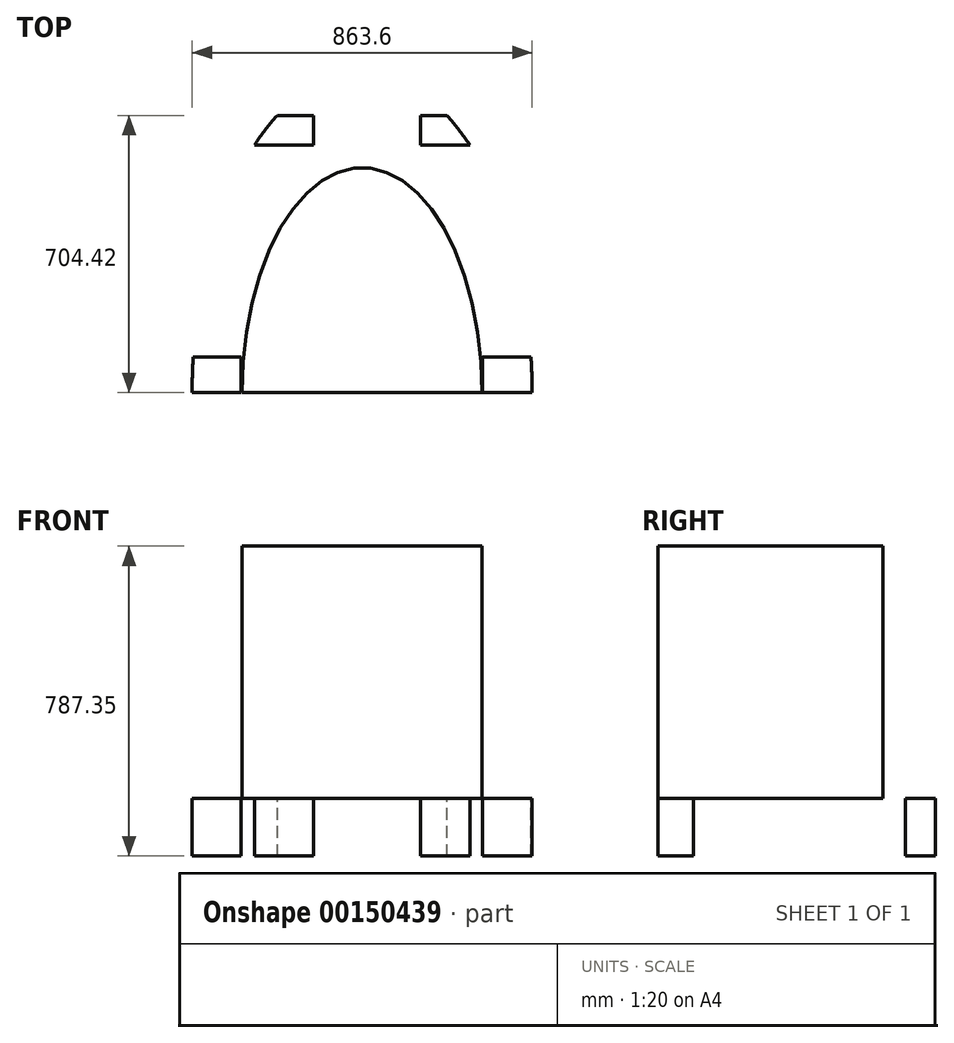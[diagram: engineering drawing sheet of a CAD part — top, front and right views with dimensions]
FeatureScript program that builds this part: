
annotation { "Feature Type Name" : "Feature", "Feature Type Description" : "" }
export const myFeature = defineFeature(function(context is Context, id is Id, definition is map)
    precondition{}
    {
        {
            var Q0;
            Q0=qCreatedBy(makeId("Top.planeOp"),FACE);
            var sketch = newSketch(context, id + "F0", { "sketchPlane" : qUnion([Q0])});
            skLineSegment(sketch, "E0", {"start": v(-431.8, 0) * mm, "end": v(431.8, 0) * mm});
            skEllipticalArc(sketch, "E1", {});
            skPoint(sketch, "E2", {"position": v(0, 812.8) * mm});
            skPoint(sketch, "E3", {"position": v(-304.8, 0) * mm});
            skPoint(sketch, "E4", {"position": v(304.8, 0) * mm});
            skPoint(sketch, "E5", {"position": v(0, 571.5) * mm});
            const initialGuessF0  = {"E1": [0, 0, 0, 1, 0.8128, 0.4318, 4.71238898038469, 1.5707963267948966], "E1": [0, 0, 0, 1, 0.5715, 0.3048, 4.71238898038469, 1.5707963267948966]};
            skSetInitialGuess(sketch, initialGuessF0);
            skSolve(sketch);
        }
        {
            var Q0;
            {var subQ0=sQuery(id+"F0.wireOp",EDGE,"E1");Q0=makeQuery(id+"F0.imprint","IMPRINT",FACE,{"disambiguationData":[TD([[makeQuery(id+"F0.imprint","IMPRINT",EDGE,{"derivedFrom":subQ0}),1.0]])]});}
            extrude(context, id + "F1", {"entities" : qUnion([Q0]), "depth" : 787.4 * mm - 501.65 * mm});
        }
        {
            var Q0;
            Q0 = qSketchRegion(id + "F0", true);
            extrude(context, id + "F2", {"entities" : qUnion([Q0]), "operationType" : NewBodyOperationType.ADD, "oppositeDirection" : true, "depth" : 355.6 * mm});
        }
        {
            var Q0;
            Q0=makeQuery(id+"F2.opExtrude","CAP_FACE",FACE,{"disambiguationData":[OSD([sQuery(id+"F0.wireOp",EDGE,"bZ2ABtPo-rZ60-tPIg-W25j-avqFfYisGgns"),sQuery(id+"F0.wireOp",EDGE,"E0")])],"isStart":false});
            var sketch = newSketch(context, id + "F3", { "sketchPlane" : qUnion([Q0])});
            skEllipticalArc(sketch, "E6.0", {});
            skLineSegment(sketch, "E7.0", {"start": v(-431.8, 0) * mm, "end": v(-307.65, 0) * mm});
            skLineSegment(sketch, "E8", {"start": v(-429.13, -90.23) * mm, "end": v(-307.65, -90.23) * mm});
            skLineSegment(sketch, "E9", {"start": v(306.2, 0) * mm, "end": v(306.2, -90.23) * mm});
            skLineSegment(sketch, "E10", {"start": v(-307.65, 0) * mm, "end": v(-307.65, -90.23) * mm});
            skLineSegment(sketch, "E11", {"start": v(215.43, -704.42) * mm, "end": v(147.86, -704.42) * mm});
            skLineSegment(sketch, "E12", {"start": v(273.47, -629) * mm, "end": v(147.86, -629) * mm});
            skLineSegment(sketch, "E13", {"start": v(-123.88, -704.42) * mm, "end": v(-123.88, -629) * mm});
            skLineSegment(sketch, "E14", {"start": v(147.86, -704.42) * mm, "end": v(147.86, -629) * mm});
            skLineSegment(sketch, "E15.trimOffspring", {"start": v(306.2, 0) * mm, "end": v(431.8, 0) * mm});
            skLineSegment(sketch, "E16.trimOffspring", {"start": v(306.2, -90.23) * mm, "end": v(429.13, -90.23) * mm});
            skEllipticalArc(sketch, "E17.trimOffspring", {});
            skEllipticalArc(sketch, "E18.trimOffspring", {});
            skLineSegment(sketch, "E19.trimOffspring", {"start": v(-123.88, -629) * mm, "end": v(-273.47, -629) * mm});
            skLineSegment(sketch, "E20.trimOffspring", {"start": v(-123.88, -704.42) * mm, "end": v(-215.43, -704.42) * mm});
            skEllipticalArc(sketch, "E21.trimOffspring", {});
            const initialGuessF3  = {"E6.0": [0, 0, 0, -1, 0.8128, 0.4318, 4.71238898038469, 4.823633551072674], "E17.trimOffspring": [0, 0, 0, -1, 0.8128, 0.4318, 5.597329593967603, 5.760846120406384], "E18.trimOffspring": [0, 0, 0, -1, 0.8128, 0.4318, 1.4595517561069133, 1.5707963267948966], "E21.trimOffspring": [0, 0, 0, -1, 0.8128, 0.4318, 0.5223391867732028, 0.6858557132119829]};
            skSetInitialGuess(sketch, initialGuessF3);
            skSolve(sketch);
        }
        {
            var Q0;
            Q0 = qSketchRegion(id + "F3", true);
            extrude(context, id + "F4", {"entities" : qUnion([Q0]), "operationType" : NewBodyOperationType.ADD, "depth" : 146 * mm});
        }
    });
